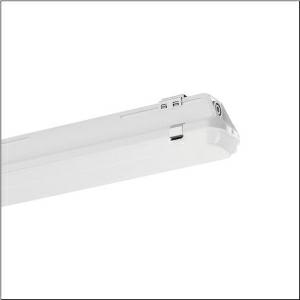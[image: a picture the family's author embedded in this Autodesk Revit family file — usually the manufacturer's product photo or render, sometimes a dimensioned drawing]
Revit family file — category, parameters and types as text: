
# Revit family: monsun_r__11_51fp10ep430l007_4604
name_source: partatom
category: Lighting Fixtures
units: mm (PartAtom-declared; Revit-internal decimal feet)

## family parameters
Cut with Voids When Loaded = No
Host = Face
Light Source = No
Part Type = Normal
Room Calculation Point = No
Round Connector Dimension = Use Diameter
Shared = No

## types (1)
- --- (1 x LED, 3840 lm, 20.5 W, 4000K)
    Apparent Load = 21 VA
    CIE Flux Codes = 47 77 93 94 100
    Color Rendering = 80
    Color Temperature = 4000K
    Default Elevation = 1800 mm
    Description = Monsun® 11, damp-proof luminaire, chain hanger, primary optical cover: enclosure, of PMMA, light emission: direct distribution, primary light characteristic: symmetric, installation type: suspended mounting, surface-mounted, horizontal mounting, vertical mounting, LED, rated luminous flux: 3.840lm, luminous efficacy: 187lm/W, light colour: 840, colour temperature: 4000K, control gear: DALI 2, with terminal, 5-pole, max. 2.5mm², through-wiring: 7x 2.5mm², mains connection: 220..240V, AC, 50/60Hz, rated input power: 21W, housing, of glass-fibre reinforced polyester, uncoated, bright grey, incl. chain hanger, length: 1.590mm, width: 90mm, height: 88mm, clip for enclosure, of stainless steel (V2A), ceiling mounting element, of stainless steel (V2A), chain hanger, of stainless steel (V2A), protection rating (complete): IP66, insulation class (complete): insulation class I (protective earthing), certification: CE, ENEC, VDE, UKCA, protection symbol: D, impact resistance: IK04, permissible operating ambient temperature: -25..+40°C, standard: EN 50419, EN 60598-2-1, corresponds to IFS (International Featured Standards) requirements for safety and quality in the food industry, for indoor or canopied outdoor use, no direct snow, no direct sun, no direct rain, LABS conformity tested according to VDMA 24364:2018-05, contact your sales advisor before using the luminaires in applications with unclear chemical exposure, large temperature fluctuations or condensation-forming humidity, packaging unit: 1 piece
    Height = 89 mm
    Lamp = 1 x LED
    Lamp Light Flux = 3840 lm
    Lamp Power = 20.5 W
    Lamp count = 1
    Length = 1590 mm
    Luminous efficacy = 187 lm/W
    Manufacturer = Siteco
    ModVariant = No
    Model = 51FP10EP430L007
    Mounting Place = Ceiling
    Mounting Type = Surface mounted
    Number of Poles = 1
    OnlyDefault = Yes
    Power Factor = 1
    Product Name = Monsun® 11
    Product group = damp-proof luminaire
    ProductGroupID = 301
    Protection Class = Protection class I
    Protection Degree = IP 66
    RLX_Detail_Level = 1
    RLX_Emergency_Light_Flux = 0 lm
    RLX_Emergency_Type = 0
    RLX_Emergency_Type_DB = No
    RlxData = <blob elided: 92101 chars, md5=fc8c885c>
    Socket = socket
    Standby Power = 0 W
    System Light Flux = 3840 lm
    System Power = 21 W
    Type Comments = factory setting: luminous flux: 100 % | dim-lin: 254 | 136 mA
    Type Image = l_1349237.jpg
    URL = http://relux.com
    VarID = @adj_037833
    Voltage = 0 V
    Weight = 0.00 kg
    Width = 90 mm

## geometry (parser evidence)
native form markers: Blend x4, Sweep x13
no freeform markers — native parametric forms only
